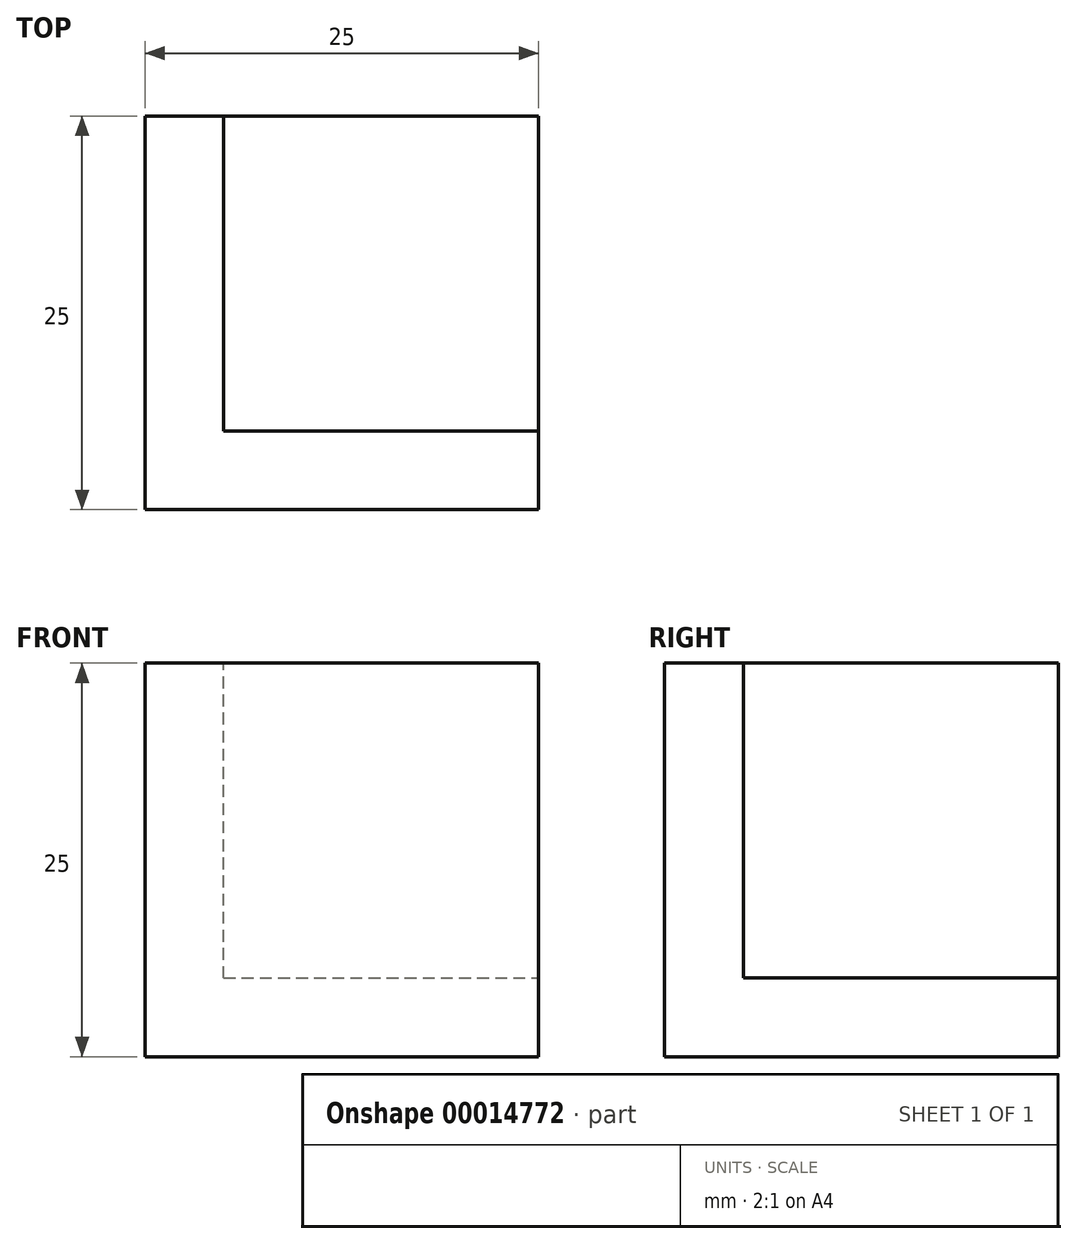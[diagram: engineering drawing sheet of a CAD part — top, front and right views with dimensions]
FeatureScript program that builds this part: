
annotation { "Feature Type Name" : "Feature", "Feature Type Description" : "" }
export const myFeature = defineFeature(function(context is Context, id is Id, definition is map)
    precondition{}
    {
        {
            var Q0;
            Q0=qCreatedBy(makeId("Top.planeOp"),FACE);
            var sketch = newSketch(context, id + "F0", { "sketchPlane" : qUnion([Q0])});
            skLineSegment(sketch, "E0.bottom", {"start": v(-12.87, 14.16) * mm, "end": v(12.13, 14.16) * mm});
            skLineSegment(sketch, "E0.top", {"start": v(-12.87, -10.84) * mm, "end": v(12.13, -10.84) * mm});
            skLineSegment(sketch, "E0.left", {"start": v(-12.87, 14.16) * mm, "end": v(-12.87, -10.84) * mm});
            skLineSegment(sketch, "E0.right", {"start": v(12.13, 14.16) * mm, "end": v(12.13, -10.84) * mm});
            skSolve(sketch);
        }
        {
            var Q0;
            Q0=makeQuery(id+"F0.imprint","IMPRINT",FACE,{"disambiguationData":[TD([[makeQuery(id+"F0.imprint","IMPRINT",EDGE,{"derivedFrom":sQuery(id+"F0.wireOp",EDGE,"E0.bottom")}),-1.0]])]});
            extrude(context, id + "F1", {"entities" : qUnion([Q0]), "depth" : 25 * mm});
        }
        {
            var Q0;
            Q0=makeQuery(id+"F1.opExtrude","CAP_FACE",FACE,{"disambiguationData":[OSD([sQuery(id+"F0.wireOp",EDGE,"E0.bottom"),sQuery(id+"F0.wireOp",EDGE,"E0.top"),sQuery(id+"F0.wireOp",EDGE,"E0.left"),sQuery(id+"F0.wireOp",EDGE,"E0.right")])],"isStart":false});
            var sketch = newSketch(context, id + "F2", { "sketchPlane" : qUnion([Q0])});
            skLineSegment(sketch, "E1", {"start": v(-7.87, 14.16) * mm, "end": v(-7.87, -5.84) * mm});
            skLineSegment(sketch, "E2", {"start": v(-7.87, -5.84) * mm, "end": v(12.13, -5.84) * mm});
            skLineSegment(sketch, "E3", {"start": v(12.13, -5.84) * mm, "end": v(12.13, 14.16) * mm});
            skLineSegment(sketch, "E4", {"start": v(12.13, 14.16) * mm, "end": v(-7.87, 14.16) * mm});
            skSolve(sketch);
        }
        {
            var Q0;
            Q0=makeQuery(id+"F2.imprint","IMPRINT",FACE,{"disambiguationData":[TD([[makeQuery(id+"F2.imprint","IMPRINT",EDGE,{"derivedFrom":sQuery(id+"F2.wireOp",EDGE,"E1")}),1.0]])]});
            extrude(context, id + "F3", {"entities" : qUnion([Q0]), "operationType" : NewBodyOperationType.REMOVE, "oppositeDirection" : true, "depth" : 20 * mm});
        }
    });
